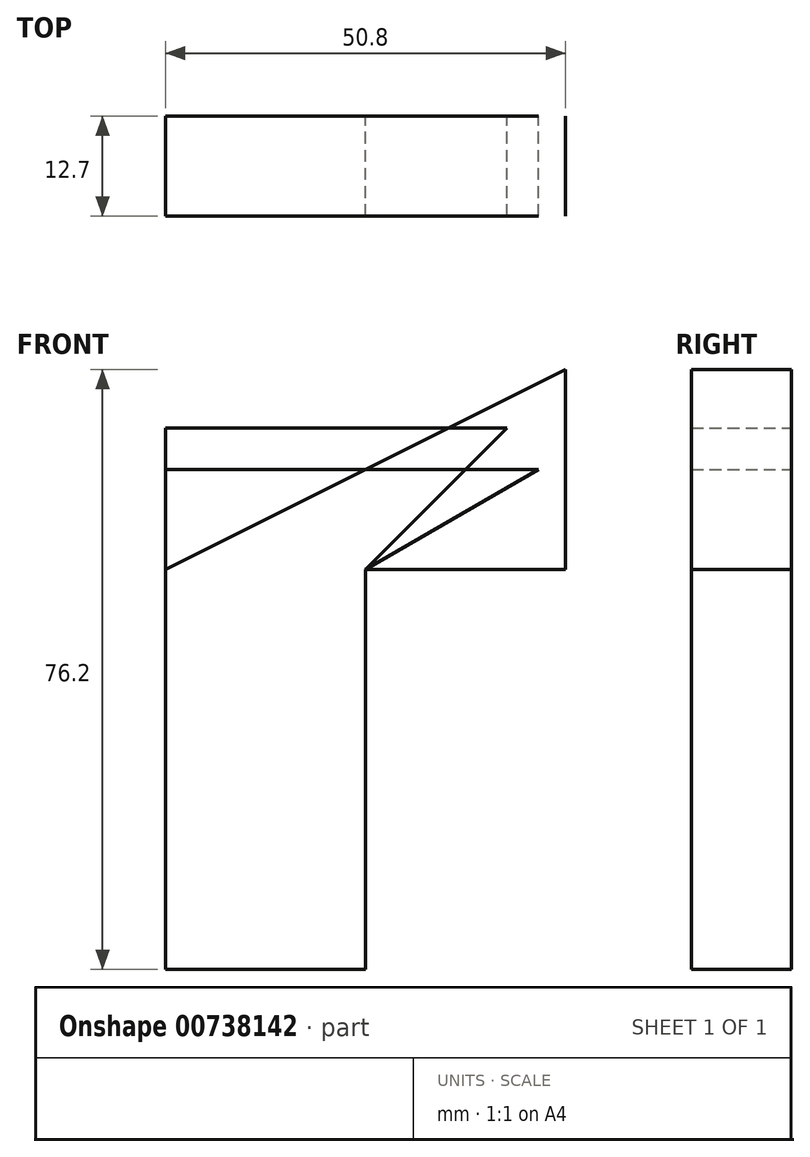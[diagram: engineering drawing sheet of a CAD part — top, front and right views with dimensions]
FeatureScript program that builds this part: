
annotation { "Feature Type Name" : "Feature", "Feature Type Description" : "" }
export const myFeature = defineFeature(function(context is Context, id is Id, definition is map)
    precondition{}
    {
        {
            var Q0;
            Q0=qCreatedBy(makeId("Front.planeOp"),FACE);
            var sketch = newSketch(context, id + "F0", { "sketchPlane" : qUnion([Q0])});
            skLineSegment(sketch, "E0.bottom", {"start": v(12.7, 25.4) * mm, "end": v(-12.7, 25.4) * mm});
            skLineSegment(sketch, "E0.top", {"start": v(12.7, -25.4) * mm, "end": v(-12.7, -25.4) * mm});
            skLineSegment(sketch, "E0.left", {"start": v(12.7, 25.4) * mm, "end": v(12.7, -25.4) * mm});
            skLineSegment(sketch, "E0.right", {"start": v(-12.7, 25.4) * mm, "end": v(-12.7, -25.4) * mm});
            skPoint(sketch, "E0.middle", {"position": v(0, 0) * mm});
            skLineSegment(sketch, "E1", {"start": v(12.7, 25.4) * mm, "end": v(38.1, 25.4) * mm});
            skLineSegment(sketch, "E2", {"start": v(38.1, 25.4) * mm, "end": v(38.1, 50.8) * mm});
            skLineSegment(sketch, "E3", {"start": v(-12.7, 25.4) * mm, "end": v(38.1, 50.8) * mm});
            skLineSegment(sketch, "E4", {"start": v(12.7, -25.4) * mm, "end": v(38.1, 25.4) * mm, "construction": true});
            skSolve(sketch);
        }
        {
            var Q0;
            Q0=makeQuery(id+"F0.imprint","IMPRINT",FACE,{"disambiguationData":[TD([[makeQuery(id+"F0.imprint","IMPRINT",EDGE,{"derivedFrom":sQuery(id+"F0.wireOp",EDGE,"E0.bottom")}),1.0]])]});
            var Q1;
            Q1=makeQuery(id+"F0.imprint","IMPRINT",FACE,{"disambiguationData":[TD([[makeQuery(id+"F0.imprint","IMPRINT",EDGE,{"derivedFrom":sQuery(id+"F0.wireOp",EDGE,"E0.bottom")}),-1.0]])]});
            extrude(context, id + "F1", {"entities" : qUnion([Q0, Q1]), "endBound" : BoundingType.SYMMETRIC, "depth" : 12.7 * mm, "offsetDistance" : 25.4 * mm});
        }
        {
            var Q0;
            Q0=qCreatedBy(makeId("Front.planeOp"),FACE);
            var sketch = newSketch(context, id + "F2", { "sketchPlane" : qUnion([Q0])});
            skLineSegment(sketch, "E5.bottom", {"start": v(12.7, 25.4) * mm, "end": v(-12.7, 25.4) * mm});
            skLineSegment(sketch, "E5.top", {"start": v(12.7, -25.4) * mm, "end": v(-12.7, -25.4) * mm});
            skLineSegment(sketch, "E5.left", {"start": v(12.7, 25.4) * mm, "end": v(12.7, -25.4) * mm});
            skLineSegment(sketch, "E5.right", {"start": v(-12.7, 25.4) * mm, "end": v(-12.7, -25.4) * mm});
            skPoint(sketch, "E5.middle", {"position": v(0, 0) * mm});
            skLineSegment(sketch, "E6", {"start": v(12.7, 25.4) * mm, "end": v(34.7, 38.1) * mm});
            skLineSegment(sketch, "E7", {"start": v(34.7, 38.1) * mm, "end": v(-12.7, 38.1) * mm});
            skLineSegment(sketch, "E8", {"start": v(-12.7, 25.4) * mm, "end": v(-12.7, 38.1) * mm});
            skLineSegment(sketch, "E9", {"start": v(12.7, -25.4) * mm, "end": v(34.7, 38.1) * mm, "construction": true});
            skSolve(sketch);
        }
        {
            var Q0;
            Q0=makeQuery(id+"F2.imprint","IMPRINT",FACE,{"disambiguationData":[TD([[makeQuery(id+"F2.imprint","IMPRINT",EDGE,{"derivedFrom":sQuery(id+"F2.wireOp",EDGE,"E5.bottom")}),1.0]])]});
            var Q1;
            Q1=makeQuery(id+"F2.imprint","IMPRINT",FACE,{"disambiguationData":[TD([[makeQuery(id+"F2.imprint","IMPRINT",EDGE,{"derivedFrom":sQuery(id+"F2.wireOp",EDGE,"E5.bottom")}),-1.0]])]});
            extrude(context, id + "F3", {"entities" : qUnion([Q0, Q1]), "endBound" : BoundingType.SYMMETRIC, "depth" : 12.7 * mm, "offsetDistance" : 25.4 * mm});
        }
        {
            var Q0;
            Q0=qCreatedBy(makeId("Front.planeOp"),FACE);
            var sketch = newSketch(context, id + "F4", { "sketchPlane" : qUnion([Q0])});
            skLineSegment(sketch, "E10.bottom", {"start": v(12.7, 25.4) * mm, "end": v(-12.7, 25.4) * mm});
            skLineSegment(sketch, "E10.top", {"start": v(12.7, -25.4) * mm, "end": v(-12.7, -25.4) * mm});
            skLineSegment(sketch, "E10.left", {"start": v(12.7, 25.4) * mm, "end": v(12.7, -25.4) * mm});
            skLineSegment(sketch, "E10.right", {"start": v(-12.7, 25.4) * mm, "end": v(-12.7, -25.4) * mm});
            skPoint(sketch, "E10.middle", {"position": v(0, 0) * mm});
            skLineSegment(sketch, "E11", {"start": v(12.7, 25.4) * mm, "end": v(30.66, 43.36) * mm});
            skLineSegment(sketch, "E12", {"start": v(30.66, 43.36) * mm, "end": v(-12.7, 43.36) * mm});
            skLineSegment(sketch, "E13", {"start": v(-12.7, 43.36) * mm, "end": v(-12.7, 43.36) * mm});
            skLineSegment(sketch, "E14", {"start": v(-12.7, 43.36) * mm, "end": v(-12.7, 25.4) * mm});
            skLineSegment(sketch, "E15", {"start": v(30.66, 43.36) * mm, "end": v(12.7, -25.4) * mm, "construction": true});
            skLineSegment(sketch, "E16", {"start": v(30.66, 43.36) * mm, "end": v(25.98, 25.45) * mm});
            skLineSegment(sketch, "E17", {"start": v(25.98, 25.45) * mm, "end": v(30.66, 43.36) * mm});
            skSolve(sketch);
        }
        {
            var Q0;
            Q0=makeQuery(id+"F4.imprint","IMPRINT",FACE,{"disambiguationData":[TD([[makeQuery(id+"F4.imprint","IMPRINT",EDGE,{"derivedFrom":sQuery(id+"F4.wireOp",EDGE,"E10.bottom")}),-1.0]])]});
            var Q1;
            Q1=makeQuery(id+"F4.imprint","IMPRINT",FACE,{"disambiguationData":[TD([[makeQuery(id+"F4.imprint","IMPRINT",EDGE,{"derivedFrom":sQuery(id+"F4.wireOp",EDGE,"E10.bottom")}),1.0]])]});
            extrude(context, id + "F5", {"entities" : qUnion([Q0, Q1]), "endBound" : BoundingType.SYMMETRIC, "depth" : 12.7 * mm, "offsetDistance" : 25.4 * mm});
        }
    });
